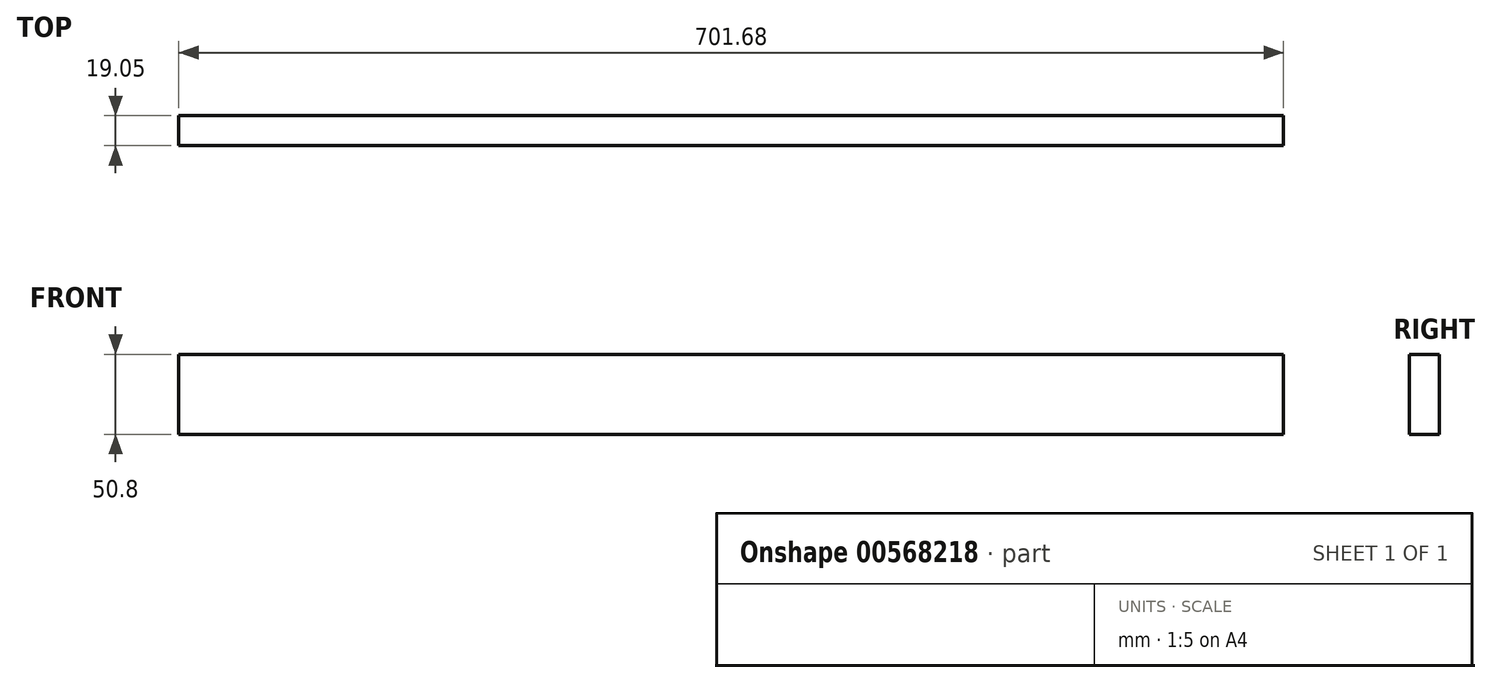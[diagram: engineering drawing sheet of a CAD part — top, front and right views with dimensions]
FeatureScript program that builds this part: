
annotation { "Feature Type Name" : "Feature", "Feature Type Description" : "" }
export const myFeature = defineFeature(function(context is Context, id is Id, definition is map)
    precondition{}
    {
        {
            var Q0;
            Q0=qCreatedBy(makeId("Front.planeOp"),FACE);
            var sketch = newSketch(context, id + "F0", { "sketchPlane" : qUnion([Q0])});
            skLineSegment(sketch, "E0.bottom", {"start": v(0, 0) * mm, "end": v(701.68, 0) * mm});
            skLineSegment(sketch, "E0.top", {"start": v(0, 50.8) * mm, "end": v(701.68, 50.8) * mm});
            skLineSegment(sketch, "E0.left", {"start": v(0, 0) * mm, "end": v(0, 50.8) * mm});
            skLineSegment(sketch, "E0.right", {"start": v(701.68, 0) * mm, "end": v(701.68, 50.8) * mm});
            skSolve(sketch);
        }
        {
            var Q0;
            Q0=makeQuery(id+"F0.imprint","IMPRINT",FACE,{"disambiguationData":[TD([[makeQuery(id+"F0.imprint","IMPRINT",EDGE,{"derivedFrom":sQuery(id+"F0.wireOp",EDGE,"E0.bottom")}),1.0]])]});
            extrude(context, id + "F1", {"entities" : qUnion([Q0]), "depth" : 19.05 * mm, "offsetDistance" : 25.4 * mm});
        }
    });
